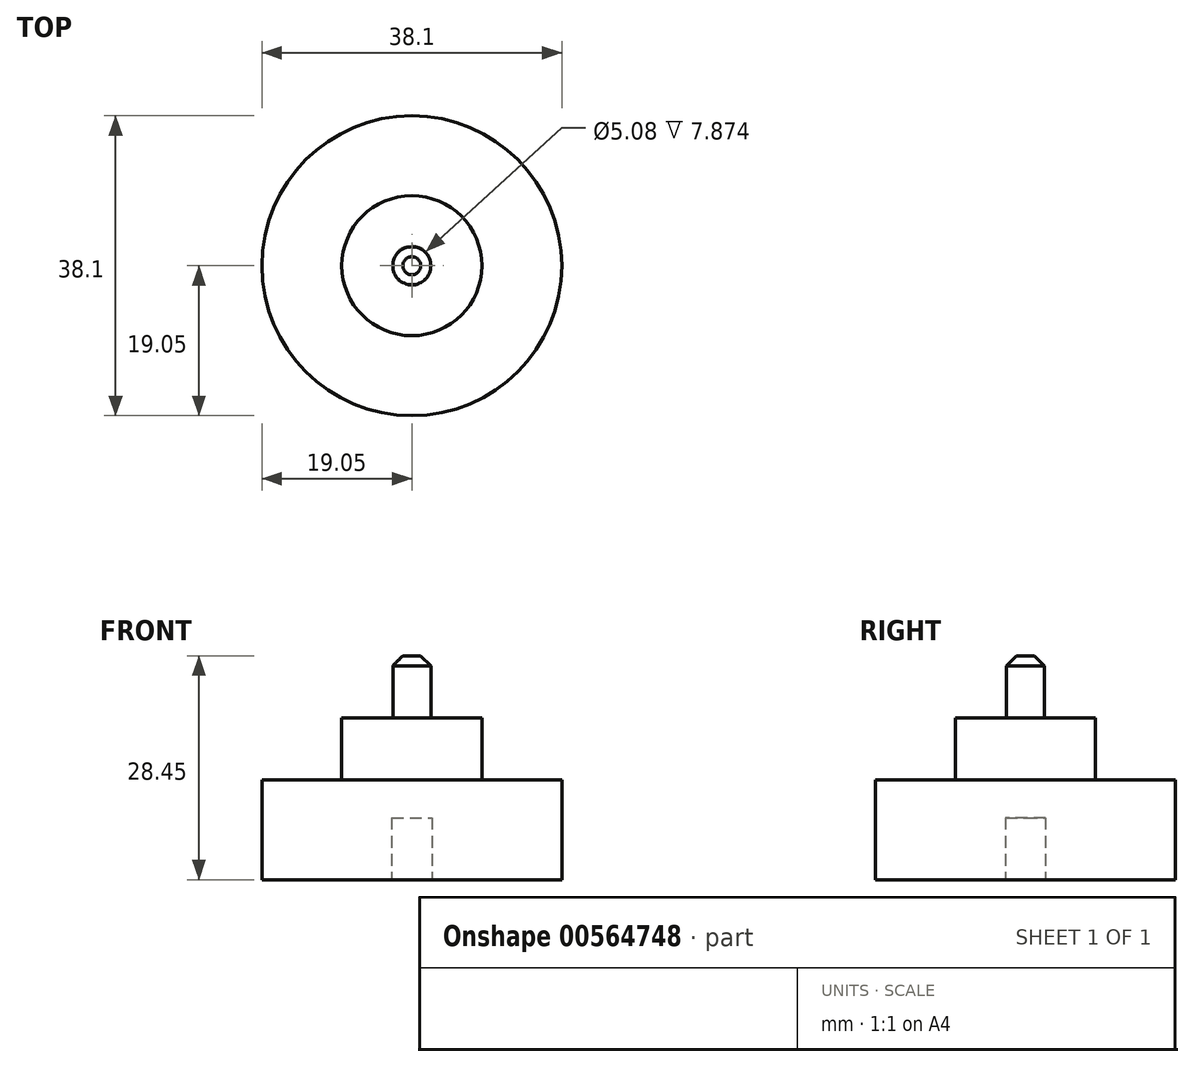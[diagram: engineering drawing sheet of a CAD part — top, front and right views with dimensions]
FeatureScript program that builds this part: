
annotation { "Feature Type Name" : "Feature", "Feature Type Description" : "" }
export const myFeature = defineFeature(function(context is Context, id is Id, definition is map)
    precondition{}
    {
        {
            var Q0;
            Q0=qCreatedBy(makeId("Front.planeOp"),FACE);
            var sketch = newSketch(context, id + "F0", { "sketchPlane" : qUnion([Q0])});
            skLineSegment(sketch, "E0", {"start": v(19.05, 0) * mm, "end": v(19.05, 12.7) * mm});
            skLineSegment(sketch, "E1", {"start": v(19.05, 12.7) * mm, "end": v(8.9, 12.7) * mm});
            skLineSegment(sketch, "E2", {"start": v(2.41, 20.57) * mm, "end": v(8.9, 20.57) * mm});
            skLineSegment(sketch, "E3", {"start": v(8.9, 20.57) * mm, "end": v(8.9, 12.7) * mm});
            skLineSegment(sketch, "E4", {"start": v(0, 28.45) * mm, "end": v(2.41, 28.45) * mm});
            skLineSegment(sketch, "E5", {"start": v(2.41, 28.45) * mm, "end": v(2.41, 20.57) * mm});
            skPoint(sketch, "E6.start.orphan", {"position": v(0, 12.7) * mm});
            skLineSegment(sketch, "E7", {"start": v(0, 0) * mm, "end": v(2.54, 0) * mm});
            skLineSegment(sketch, "E8", {"start": v(2.54, 0) * mm, "end": v(2.54, 7.87) * mm});
            skLineSegment(sketch, "E9", {"start": v(2.54, 7.87) * mm, "end": v(0, 7.87) * mm});
            skLineSegment(sketch, "E10", {"start": v(0, 7.87) * mm, "end": v(0, 28.45) * mm});
            skLineSegment(sketch, "E11", {"start": v(2.54, 0) * mm, "end": v(19.05, 0) * mm});
            skSolve(sketch);
        }
        {
            var Q0;
            Q0 = qSketchRegion(id + "F0", true);
            var Q1;
            Q1=sQuery(id+"F0.wireOp",EDGE,"E10");
            revolve(context, id + "F1", {"entities" : qUnion([Q0]), "axis" : qUnion([Q1]), "revolveType" : RevolveType.FULL});
        }
        {
            var Q0;
            Q0=makeQuery(id+"F1.opRevolve","SWEPT_EDGE",EDGE,{"disambiguationData":[OSD([sQuery(id+"F0.wireOp",EDGE,"E4"),sQuery(id+"F0.wireOp",EDGE,"E5")])]});
            chamfer(context, id + "F2", {"entities" : qUnion([Q0]), "width" : 1.27 * mm, "tangentPropagation" : true});
        }
    });
